# Revit family: SPG1012-4_Revit
name_source: partatom
category: Mechanical Equipment
revit_build: Autodesk Revit 2014 (Build: 20130215_1615(x64)
units: mm (PartAtom-declared; Revit-internal decimal feet)

## types (1)
- Standard
    Connector_10_Diameter = 0' - 0"
    Connector_15_Diameter = 0' - 0"
    Connector_16_Diameter = 0' - 0"
    Connector_17_Diameter = 0' - 0"
    Connector_18_Diameter = 0' - 0"
    Connector_19_Diameter = 0' - 0"
    Connector_1_Diameter = 0' - 0"
    Connector_20_Diameter = 0' - 0"
    Connector_21_Diameter = 0' - 0"
    Connector_22_Height = 0' - 0"
    Connector_22_Width = 0' - 0"
    Connector_23_Height = 0' - 0"
    Connector_23_Width = 0' - 0"
    Connector_24_Height = 0' - 0"
    Connector_24_Width = 0' - 0"
    Connector_25_Height = 0' - 0"
    Connector_25_Width = 0' - 0"
    Connector_2_Diameter = 0' - 0"
    Connector_3_Diameter = 0' - 0"
    Connector_4_Diameter = 0' - 0"
    Connector_5_Diameter = 0' - 0"
    Connector_6_Diameter = 0' - 0"
    Connector_7_Diameter = 0' - 0"
    Connector_8_Diameter = 0' - 0"
    Connector_9_Diameter = 0' - 0"
    Description = Gas Fired Humidifier (4 Modules)
    Design Status = 1
    Manufacturer = Neptronic
    Model = SKG3710, SKG3765, SKG3810
    Part Number = SPG1012-4_Revit
    URL = www.neptronic.com
    d100 = 0' - 2 1/32"
    d102 = 0' - 2 5/16"
    d104 = 0' - 2 5/16"
    d106 = 3' - 8 15/16"
    d108 = 3' - 8 15/16"
    d110 = 3' - 8 15/16"
    d112 = 3' - 8 15/16"
    d114 = 3' - 9 3/16"
    d116 = 0' - 5"
    d118 = 0' - 5"
    d120 = 0' - 5"
    d122 = 0' - 5"
    d124 = 0' - 5 1/4"
    d126 = 4' - 4"
    d132 = 0' - 0"
    d16 = 0' - 0 1/2"
    d18 = 0' - 0 1/2"
    d20 = 0' - 0 1/2"
    d22 = 0' - 0 1/2"
    d24 = 0' - 0 1/2"
    d26 = 0' - 0 1/2"
    d28 = 0' - 0 1/2"
    d30 = 0' - 0 1/2"
    d32 = 0' - 0 1/2"
    d34 = 0' - 0 1/2"
    d36 = 0' - 0 1/2"
    d38 = 0' - 0 1/2"
    d40 = 0' - 0 1/2"
    d42 = 0' - 0 1/2"
    d44 = 0' - 1 9/16"
    d46 = 0' - 0 1/2"
    d48 = 0' - 0 1/2"
    d50 = 0' - 0 1/2"
    d52 = 0' - 0 1/2"
    d54 = 0' - 0 1/2"
    d56 = 0' - 0 1/2"
    d58 = 0' - 0 1/2"
    d60 = 0' - 0 1/2"
    d62 = 0' - 0 1/2"
    d64 = 0' - 0 1/2"
    d66 = 0' - 0 1/2"
    d68 = 0' - 0 1/2"
    d70 = 0' - 0 1/2"
    d72 = 0' - 2 1/32"
    d74 = 0' - 2 1/32"
    d76 = 0' - 2 1/32"
    d78 = 0' - 2 1/32"
    d80 = 0' - 2 1/32"
    d82 = 0' - 2 1/32"
    d84 = 0' - 2 1/32"
    d86 = 0' - 2 1/32"
    d88 = 0' - 2 1/32"
    d90 = 0' - 2 1/32"
    d92 = 0' - 2 1/32"
    d94 = 0' - 2 1/32"
    d96 = 0' - 2 1/32"
    d98 = 0' - 2 1/32"

## geometry (parser evidence)
native form markers: Sweep x2
no freeform markers — native parametric forms only
